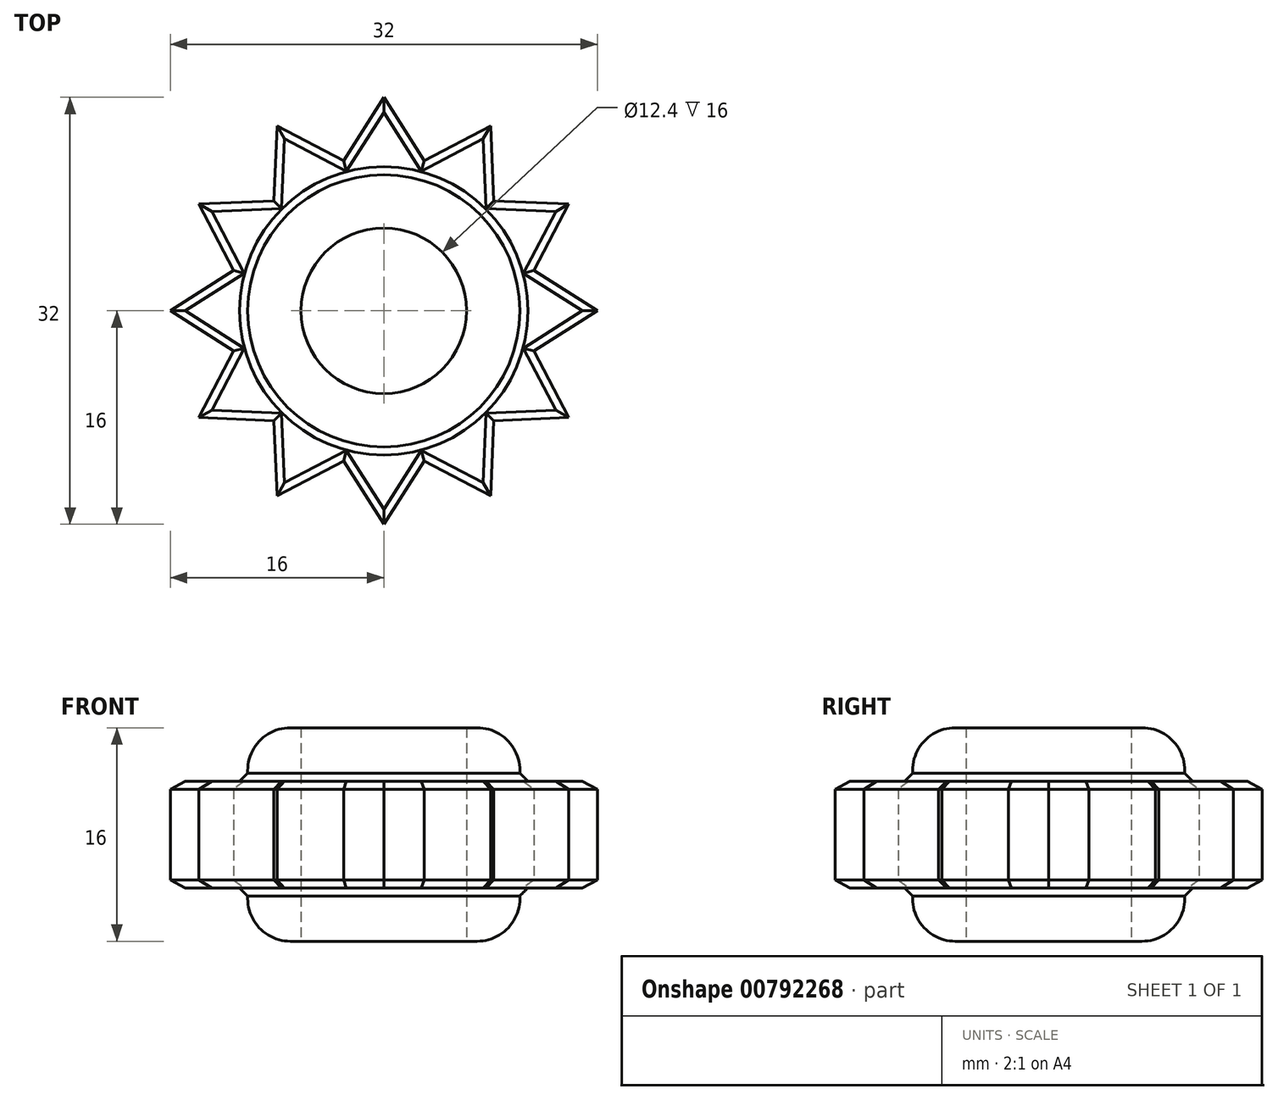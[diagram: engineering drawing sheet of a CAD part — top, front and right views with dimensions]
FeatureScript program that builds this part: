
annotation { "Feature Type Name" : "Feature", "Feature Type Description" : "" }
export const myFeature = defineFeature(function(context is Context, id is Id, definition is map)
    precondition{}
    {
        {
            var Q0;
            Q0=qCreatedBy(makeId("Top.planeOp"),FACE);
            var sketch = newSketch(context, id + "F0", { "sketchPlane" : qUnion([Q0])});
            skCircle(sketch, "E0", {"center": v(0, 0) * mm, "radius": 3.1 * mm});
            skCircle(sketch, "E1", {"center": v(0, 0) * mm, "radius": 5.1 * mm});
            skLineSegment(sketch, "E2", {"start": v(0, 0) * mm, "end": v(0, 8) * mm});
            skLineSegment(sketch, "E3", {"start": v(0, 0) * mm, "end": v(8, 0) * mm});
            skLineSegment(sketch, "E4", {"start": v(0, 0) * mm, "end": v(0, -8) * mm});
            skLineSegment(sketch, "E5", {"start": v(0, 0) * mm, "end": v(-8, 0) * mm});
            skLineSegment(sketch, "E6", {"start": v(0, 8) * mm, "end": v(-2.15, 4.63) * mm});
            skLineSegment(sketch, "E7", {"start": v(0, 8) * mm, "end": v(2.15, 4.63) * mm});
            skLineSegment(sketch, "E8.1.1", {"start": v(8, 0) * mm, "end": v(4.63, 2.15) * mm});
            skLineSegment(sketch, "E8.1.2", {"start": v(8, 0) * mm, "end": v(4.63, -2.15) * mm});
            skLineSegment(sketch, "E8.2.1", {"start": v(0, -8) * mm, "end": v(2.15, -4.63) * mm});
            skLineSegment(sketch, "E8.2.2", {"start": v(0, -8) * mm, "end": v(-2.15, -4.63) * mm});
            skLineSegment(sketch, "E8.anchor1", {"start": v(0, 0) * mm, "end": v(-2.15, 4.63) * mm, "construction": true});
            skLineSegment(sketch, "E8.anchor2", {"start": v(0, 0) * mm, "end": v(2.15, -4.63) * mm, "construction": true});
            skLineSegment(sketch, "E9.1.1", {"start": v(-8, 0) * mm, "end": v(-4.63, -2.15) * mm});
            skLineSegment(sketch, "E9.1.2", {"start": v(-8, 0) * mm, "end": v(-4.63, 2.15) * mm});
            skLineSegment(sketch, "E9.anchor1", {"start": v(0, 0) * mm, "end": v(0, -8) * mm, "construction": true});
            skLineSegment(sketch, "E9.anchor2", {"start": v(0, 0) * mm, "end": v(0, 8) * mm, "construction": true});
            skLineSegment(sketch, "E10.1.0", {"start": v(-6.93, -4) * mm, "end": v(-5.08, -0.45) * mm});
            skLineSegment(sketch, "E10.1.1", {"start": v(-6.93, -4) * mm, "end": v(-2.93, -4.17) * mm});
            skLineSegment(sketch, "E10.1.2", {"start": v(4, -6.93) * mm, "end": v(0.45, -5.08) * mm});
            skLineSegment(sketch, "E10.1.3", {"start": v(4, -6.93) * mm, "end": v(4.17, -2.93) * mm});
            skLineSegment(sketch, "E10.1.4", {"start": v(6.93, 4) * mm, "end": v(5.08, 0.45) * mm});
            skLineSegment(sketch, "E10.1.5", {"start": v(6.93, 4) * mm, "end": v(2.93, 4.17) * mm});
            skLineSegment(sketch, "E10.1.6", {"start": v(-4, 6.93) * mm, "end": v(-0.45, 5.08) * mm});
            skLineSegment(sketch, "E10.1.7", {"start": v(-4, 6.93) * mm, "end": v(-4.17, 2.93) * mm});
            skLineSegment(sketch, "E10.2.0", {"start": v(6.93, -4) * mm, "end": v(2.93, -4.17) * mm});
            skLineSegment(sketch, "E10.2.1", {"start": v(6.93, -4) * mm, "end": v(5.08, -0.45) * mm});
            skLineSegment(sketch, "E10.2.2", {"start": v(4, 6.93) * mm, "end": v(4.17, 2.93) * mm});
            skLineSegment(sketch, "E10.2.3", {"start": v(4, 6.93) * mm, "end": v(0.45, 5.08) * mm});
            skLineSegment(sketch, "E10.2.4", {"start": v(-6.93, 4) * mm, "end": v(-2.93, 4.17) * mm});
            skLineSegment(sketch, "E10.2.5", {"start": v(-6.93, 4) * mm, "end": v(-5.08, 0.45) * mm});
            skLineSegment(sketch, "E10.2.6", {"start": v(-4, -6.93) * mm, "end": v(-4.17, -2.93) * mm});
            skLineSegment(sketch, "E10.2.7", {"start": v(-4, -6.93) * mm, "end": v(-0.45, -5.08) * mm});
            skSolve(sketch);
        }
        {
            var Q0;
            Q0 = qSketchRegion(id + "F0", true);
            extrude(context, id + "F1", {"entities" : qUnion([Q0]), "depth" : 4 * mm, "offsetDistance" : 25 * mm});
        }
        {
            var Q0;
            {var subQ1=sQuery(id+"F0.wireOp",EDGE,"E0");var subQ7=sQuery(id+"F0.wireOp",EDGE,"E2");var subQ9=makeQuery(id+"F0.imprint","INTERSECT",VERTEX,{"derivedFrom":[subQ1,subQ7]});Q0=makeQuery(id+"F0.imprint","IMPRINT",FACE,{"disambiguationData":[TD([[makeQuery(id+"F0.imprint","IMPRINT",EDGE,{"disambiguationData":[TD([[subQ9,-1.0]])],"derivedFrom":subQ1}),-1.0]])]});}
            var Q1;
            {var subQ4=sQuery(id+"F0.wireOp",EDGE,"E0");var subQ8=sQuery(id+"F0.wireOp",EDGE,"E2");var subQ9=makeQuery(id+"F0.imprint","INTERSECT",VERTEX,{"derivedFrom":[subQ4,subQ8]});Q1=makeQuery(id+"F0.imprint","IMPRINT",FACE,{"disambiguationData":[TD([[makeQuery(id+"F0.imprint","IMPRINT",EDGE,{"disambiguationData":[TD([[subQ9,1.0]])],"derivedFrom":subQ4}),-1.0]])]});}
            var Q2;
            {var subQ0=sQuery(id+"F0.wireOp",EDGE,"E5");var subQ1=sQuery(id+"F0.wireOp",EDGE,"E0");var subQ2=makeQuery(id+"F0.imprint","INTERSECT",VERTEX,{"derivedFrom":[subQ1,subQ0]});Q2=makeQuery(id+"F0.imprint","IMPRINT",FACE,{"disambiguationData":[TD([[makeQuery(id+"F0.imprint","IMPRINT",EDGE,{"disambiguationData":[TD([[subQ2,-1.0]])],"derivedFrom":subQ1}),-1.0]])]});}
            var Q3;
            {var subQ4=sQuery(id+"F0.wireOp",EDGE,"E0");var subQ7=sQuery(id+"F0.wireOp",EDGE,"E3");var subQ9=makeQuery(id+"F0.imprint","INTERSECT",VERTEX,{"derivedFrom":[subQ4,subQ7]});Q3=makeQuery(id+"F0.imprint","IMPRINT",FACE,{"disambiguationData":[TD([[makeQuery(id+"F0.imprint","IMPRINT",EDGE,{"disambiguationData":[TD([[subQ9,1.0]])],"derivedFrom":subQ4}),-1.0]])]});}
            extrude(context, id + "F2", {"entities" : qUnion([Q0, Q1, Q2, Q3]), "operationType" : NewBodyOperationType.ADD, "depth" : 6 * mm, "offsetDistance" : 25 * mm, "hasSecondDirection" : true, "secondDirectionOppositeDirection" : true, "secondDirectionDepth" : 2 * mm});
        }
        {
            var Q0;
            Q0=makeQuery(id+"F1.opExtrude","CAP_FACE",FACE,{"disambiguationData":[OSD([sQuery(id+"F0.wireOp",EDGE,"E8.1.1"),sQuery(id+"F0.wireOp",EDGE,"E8.1.2"),sQuery(id+"F0.wireOp",EDGE,"E8.2.1"),sQuery(id+"F0.wireOp",EDGE,"E8.2.2"),sQuery(id+"F0.wireOp",EDGE,"E9.1.1"),sQuery(id+"F0.wireOp",EDGE,"E9.1.2"),sQuery(id+"F0.wireOp",EDGE,"E1"),sQuery(id+"F0.wireOp",EDGE,"E6"),sQuery(id+"F0.wireOp",EDGE,"E7"),sQuery(id+"F0.wireOp",EDGE,"E10.1.0"),sQuery(id+"F0.wireOp",EDGE,"E10.1.1"),sQuery(id+"F0.wireOp",EDGE,"E10.1.2"),sQuery(id+"F0.wireOp",EDGE,"E10.1.3"),sQuery(id+"F0.wireOp",EDGE,"E10.1.4"),sQuery(id+"F0.wireOp",EDGE,"E10.1.5"),sQuery(id+"F0.wireOp",EDGE,"E10.1.6"),sQuery(id+"F0.wireOp",EDGE,"E10.1.7"),sQuery(id+"F0.wireOp",EDGE,"E10.2.0"),sQuery(id+"F0.wireOp",EDGE,"E10.2.1"),sQuery(id+"F0.wireOp",EDGE,"E10.2.2"),sQuery(id+"F0.wireOp",EDGE,"E10.2.3"),sQuery(id+"F0.wireOp",EDGE,"E10.2.4"),sQuery(id+"F0.wireOp",EDGE,"E10.2.5"),sQuery(id+"F0.wireOp",EDGE,"E10.2.6"),sQuery(id+"F0.wireOp",EDGE,"E10.2.7")])],"isStart":true});
            var Q1;
            Q1=makeQuery(id+"F1.opExtrude","CAP_FACE",FACE,{"disambiguationData":[OSD([sQuery(id+"F0.wireOp",EDGE,"E8.1.1"),sQuery(id+"F0.wireOp",EDGE,"E8.1.2"),sQuery(id+"F0.wireOp",EDGE,"E8.2.1"),sQuery(id+"F0.wireOp",EDGE,"E8.2.2"),sQuery(id+"F0.wireOp",EDGE,"E9.1.1"),sQuery(id+"F0.wireOp",EDGE,"E9.1.2"),sQuery(id+"F0.wireOp",EDGE,"E1"),sQuery(id+"F0.wireOp",EDGE,"E6"),sQuery(id+"F0.wireOp",EDGE,"E7"),sQuery(id+"F0.wireOp",EDGE,"E10.1.0"),sQuery(id+"F0.wireOp",EDGE,"E10.1.1"),sQuery(id+"F0.wireOp",EDGE,"E10.1.2"),sQuery(id+"F0.wireOp",EDGE,"E10.1.3"),sQuery(id+"F0.wireOp",EDGE,"E10.1.4"),sQuery(id+"F0.wireOp",EDGE,"E10.1.5"),sQuery(id+"F0.wireOp",EDGE,"E10.1.6"),sQuery(id+"F0.wireOp",EDGE,"E10.1.7"),sQuery(id+"F0.wireOp",EDGE,"E10.2.0"),sQuery(id+"F0.wireOp",EDGE,"E10.2.1"),sQuery(id+"F0.wireOp",EDGE,"E10.2.2"),sQuery(id+"F0.wireOp",EDGE,"E10.2.3"),sQuery(id+"F0.wireOp",EDGE,"E10.2.4"),sQuery(id+"F0.wireOp",EDGE,"E10.2.5"),sQuery(id+"F0.wireOp",EDGE,"E10.2.6"),sQuery(id+"F0.wireOp",EDGE,"E10.2.7")])],"isStart":false});
            chamfer(context, id + "F3", {"entities" : qUnion([Q0, Q1]), "width" : .3 * mm, "tangentPropagation" : true});
        }
        {
            var Q0;
            Q0=makeQuery(id+"F2.opExtrude","CAP_EDGE",EDGE,{"disambiguationData":[OSD([sQuery(id+"F0.wireOp",EDGE,"E1")])],"isStart":false});
            var Q1;
            Q1=makeQuery(id+"F2.opExtrude","CAP_EDGE",EDGE,{"disambiguationData":[OSD([sQuery(id+"F0.wireOp",EDGE,"E1")])],"isStart":true});
            fillet(context, id + "F4", {"entities" : qUnion([Q0, Q1]), "radius" : 1.6 * mm, "tangentPropagation" : true, "allowEdgeOverflow" : false});
        }
        {
            var Q0;
            Q0=makeQuery(id+"F1.opExtrude","SWEPT_BODY",BODY,{"disambiguationData":[OSD([sQuery(id+"F0.wireOp",EDGE,"E8.1.1"),sQuery(id+"F0.wireOp",EDGE,"E8.1.2"),sQuery(id+"F0.wireOp",EDGE,"E8.2.1"),sQuery(id+"F0.wireOp",EDGE,"E8.2.2"),sQuery(id+"F0.wireOp",EDGE,"E9.1.1"),sQuery(id+"F0.wireOp",EDGE,"E9.1.2"),sQuery(id+"F0.wireOp",EDGE,"E1"),sQuery(id+"F0.wireOp",EDGE,"E6"),sQuery(id+"F0.wireOp",EDGE,"E7"),sQuery(id+"F0.wireOp",EDGE,"E10.1.0"),sQuery(id+"F0.wireOp",EDGE,"E10.1.1"),sQuery(id+"F0.wireOp",EDGE,"E10.1.2"),sQuery(id+"F0.wireOp",EDGE,"E10.1.3"),sQuery(id+"F0.wireOp",EDGE,"E10.1.4"),sQuery(id+"F0.wireOp",EDGE,"E10.1.5"),sQuery(id+"F0.wireOp",EDGE,"E10.1.6"),sQuery(id+"F0.wireOp",EDGE,"E10.1.7"),sQuery(id+"F0.wireOp",EDGE,"E10.2.0"),sQuery(id+"F0.wireOp",EDGE,"E10.2.1"),sQuery(id+"F0.wireOp",EDGE,"E10.2.2"),sQuery(id+"F0.wireOp",EDGE,"E10.2.3"),sQuery(id+"F0.wireOp",EDGE,"E10.2.4"),sQuery(id+"F0.wireOp",EDGE,"E10.2.5"),sQuery(id+"F0.wireOp",EDGE,"E10.2.6"),sQuery(id+"F0.wireOp",EDGE,"E10.2.7")])]});
            var Q1;
            Q1=sQuery(id+"F0.wireOp",VERTEX,"E0.center");
            transform(context, id + "F5", {"entities" : qUnion([Q0]), "transformType" : TransformType.SCALE_UNIFORMLY, "scale" : 2, "scalePoint" : qUnion([Q1]), "makeCopy" : false});
        }
    });
